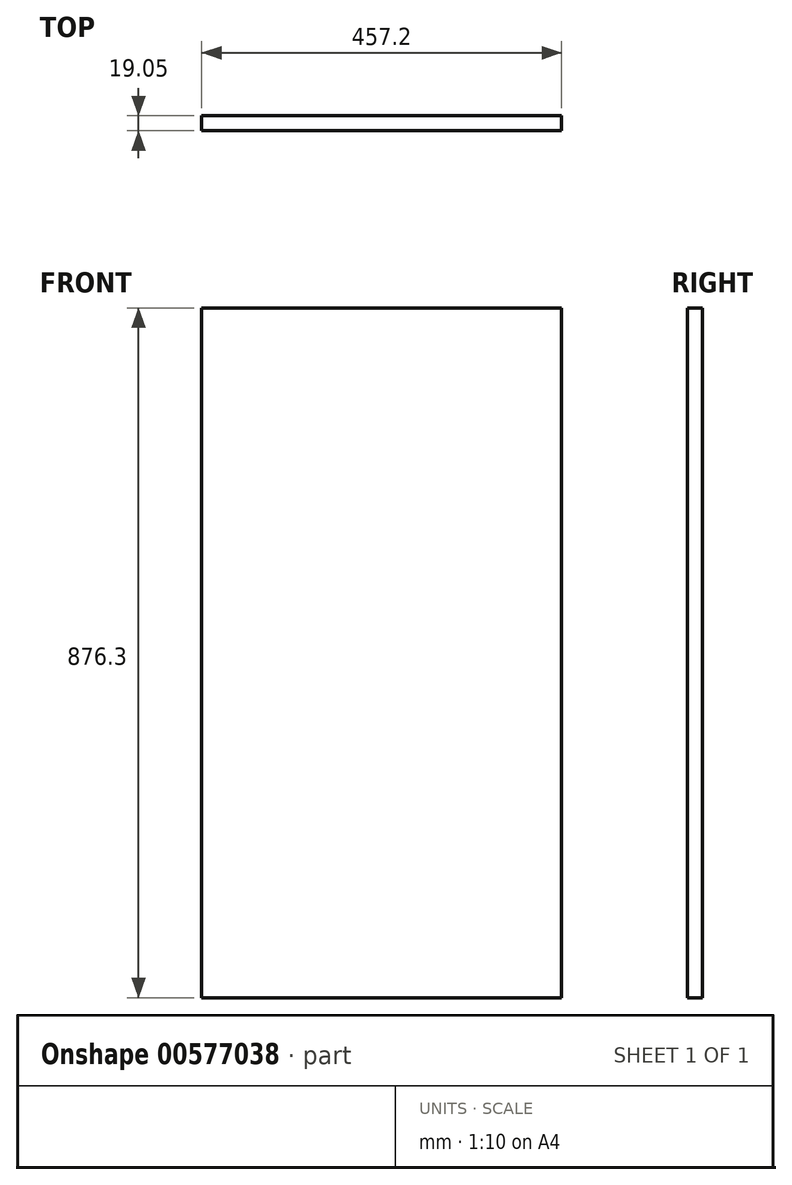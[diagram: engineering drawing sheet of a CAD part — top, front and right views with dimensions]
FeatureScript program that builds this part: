
annotation { "Feature Type Name" : "Feature", "Feature Type Description" : "" }
export const myFeature = defineFeature(function(context is Context, id is Id, definition is map)
    precondition{}
    {
        {
            var Q0;
            Q0=qCreatedBy(makeId("Front.planeOp"),FACE);
            var sketch = newSketch(context, id + "F0", { "sketchPlane" : qUnion([Q0])});
            skLineSegment(sketch, "E0.bottom", {"start": v(228.6, 438.15) * mm, "end": v(-228.6, 438.15) * mm});
            skLineSegment(sketch, "E0.top", {"start": v(228.6, -438.15) * mm, "end": v(-228.6, -438.15) * mm});
            skLineSegment(sketch, "E0.left", {"start": v(228.6, 438.15) * mm, "end": v(228.6, -438.15) * mm});
            skLineSegment(sketch, "E0.right", {"start": v(-228.6, 438.15) * mm, "end": v(-228.6, -438.15) * mm});
            skPoint(sketch, "E0.middle", {"position": v(0, 0) * mm});
            skSolve(sketch);
        }
        {
            var Q0;
            Q0=makeQuery(id+"F0.imprint","IMPRINT",FACE,{"disambiguationData":[TD([[makeQuery(id+"F0.imprint","IMPRINT",EDGE,{"derivedFrom":sQuery(id+"F0.wireOp",EDGE,"E0.bottom")}),1.0]])]});
            extrude(context, id + "F1", {"entities" : qUnion([Q0]), "depth" : 19.05 * mm, "offsetDistance" : 25.4 * mm});
        }
    });
